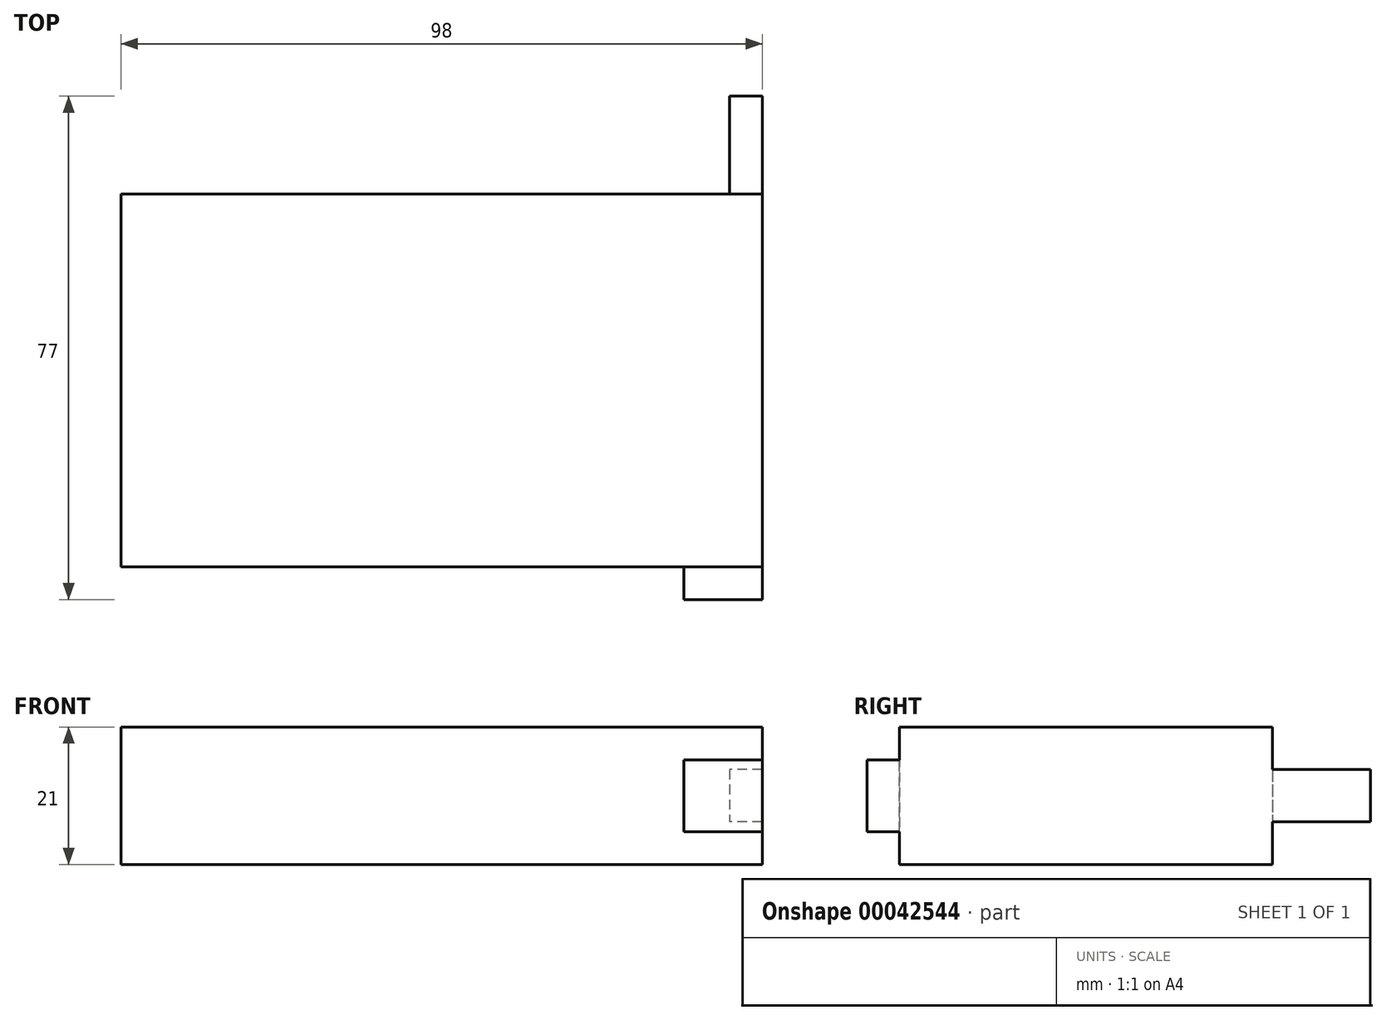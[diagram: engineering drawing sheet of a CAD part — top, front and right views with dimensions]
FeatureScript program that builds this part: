
annotation { "Feature Type Name" : "Feature", "Feature Type Description" : "" }
export const myFeature = defineFeature(function(context is Context, id is Id, definition is map)
    precondition{}
    {
        {
            var Q0;
            Q0=qCreatedBy(makeId("Top.planeOp"),FACE);
            var sketch = newSketch(context, id + "F0", { "sketchPlane" : qUnion([Q0])});
            skLineSegment(sketch, "E0.bottom", {"start": v(0, 0) * mm, "end": v(98, 0) * mm});
            skLineSegment(sketch, "E0.top", {"start": v(0, 57) * mm, "end": v(98, 57) * mm});
            skLineSegment(sketch, "E0.left", {"start": v(0, 0) * mm, "end": v(0, 57) * mm});
            skLineSegment(sketch, "E0.right", {"start": v(98, 0) * mm, "end": v(98, 57) * mm});
            skSolve(sketch);
        }
        {
            var Q0;
            Q0 = qSketchRegion(id + "F0", true);
            extrude(context, id + "F1", {"entities" : qUnion([Q0]), "depth" : 21 * mm});
        }
        {
            var Q0;
            Q0=makeQuery(id+"F1.opExtrude","SWEPT_FACE",FACE,{"disambiguationData":[OSD([sQuery(id+"F0.wireOp",EDGE,"E0.top")])]});
            var sketch = newSketch(context, id + "F2", { "sketchPlane" : qUnion([Q0])});
            skLineSegment(sketch, "E1.bottom", {"start": v(-98, 14.5) * mm, "end": v(-93, 14.5) * mm});
            skLineSegment(sketch, "E1.top", {"start": v(-98, 6.5) * mm, "end": v(-93, 6.5) * mm});
            skLineSegment(sketch, "E1.left", {"start": v(-98, 14.5) * mm, "end": v(-98, 6.5) * mm});
            skLineSegment(sketch, "E1.right", {"start": v(-93, 14.5) * mm, "end": v(-93, 6.5) * mm});
            skSolve(sketch);
        }
        {
            var Q0;
            Q0 = qSketchRegion(id + "F2", true);
            extrude(context, id + "F3", {"entities" : qUnion([Q0]), "operationType" : NewBodyOperationType.ADD, "depth" : 15 * mm});
        }
        {
            var Q0;
            Q0=makeQuery(id+"F1.opExtrude","SWEPT_FACE",FACE,{"disambiguationData":[OSD([sQuery(id+"F0.wireOp",EDGE,"E0.bottom")])]});
            var sketch = newSketch(context, id + "F4", { "sketchPlane" : qUnion([Q0])});
            skLineSegment(sketch, "E2.bottom", {"start": v(98, 5) * mm, "end": v(86, 5) * mm});
            skLineSegment(sketch, "E2.top", {"start": v(98, 16) * mm, "end": v(86, 16) * mm});
            skLineSegment(sketch, "E2.left", {"start": v(98, 5) * mm, "end": v(98, 16) * mm});
            skLineSegment(sketch, "E2.right", {"start": v(86, 5) * mm, "end": v(86, 16) * mm});
            skSolve(sketch);
        }
        {
            var Q0;
            Q0 = qSketchRegion(id + "F4", true);
            extrude(context, id + "F5", {"entities" : qUnion([Q0]), "operationType" : NewBodyOperationType.ADD, "depth" : 5 * mm});
        }
    });
